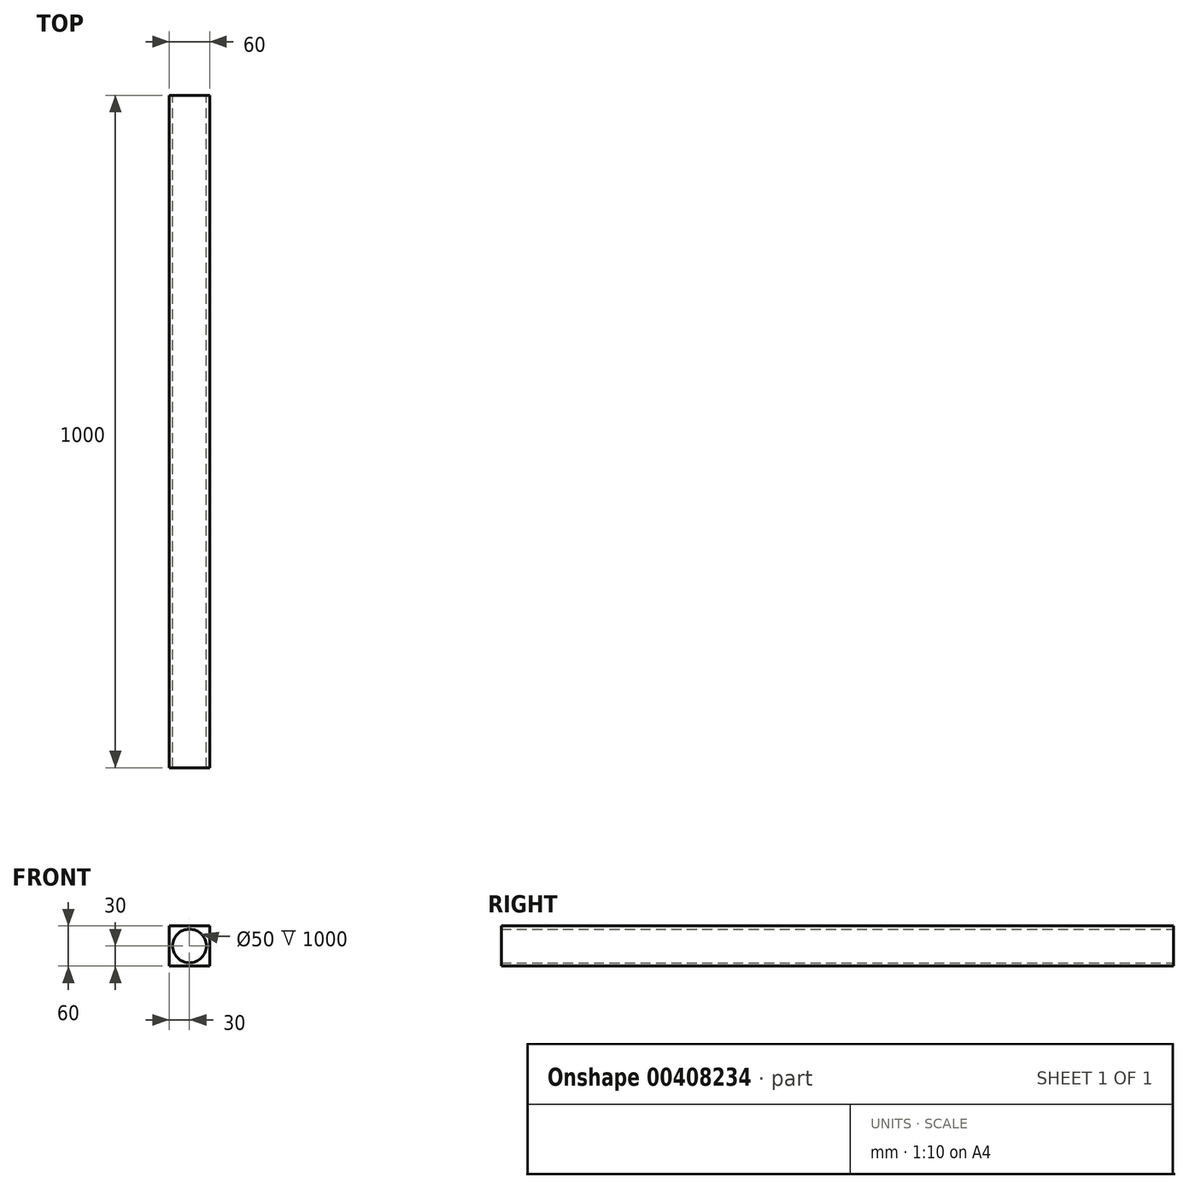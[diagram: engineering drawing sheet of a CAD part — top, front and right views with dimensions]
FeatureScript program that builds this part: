
annotation { "Feature Type Name" : "Feature", "Feature Type Description" : "" }
export const myFeature = defineFeature(function(context is Context, id is Id, definition is map)
    precondition{}
    {
        {
            var Q0;
            Q0=qCreatedBy(makeId("Front.planeOp"),FACE);
            var sketch = newSketch(context, id + "F0", { "sketchPlane" : qUnion([Q0])});
            skLineSegment(sketch, "E0", {"start": v(30, 0) * mm, "end": v(30, 30) * mm});
            skLineSegment(sketch, "E1", {"start": v(30, 30) * mm, "end": v(-30, 30) * mm});
            skLineSegment(sketch, "E2", {"start": v(-30, 30) * mm, "end": v(-30, -30) * mm});
            skLineSegment(sketch, "E3", {"start": v(-30, -30) * mm, "end": v(30, -30) * mm});
            skLineSegment(sketch, "E4", {"start": v(30, -30) * mm, "end": v(30, 0) * mm});
            skCircle(sketch, "E5", {"center": v(0, 0) * mm, "radius": 25 * mm});
            skSolve(sketch);
        }
        {
            var Q0;
            Q0=makeQuery(id+"F0.imprint","IMPRINT",FACE,{"disambiguationData":[TD([[makeQuery(id+"F0.imprint","IMPRINT",EDGE,{"derivedFrom":sQuery(id+"F0.wireOp",EDGE,"E0")}),1.0]])]});
            extrude(context, id + "F1", {"entities" : qUnion([Q0]), "depth" : 1000 * mm});
        }
    });
